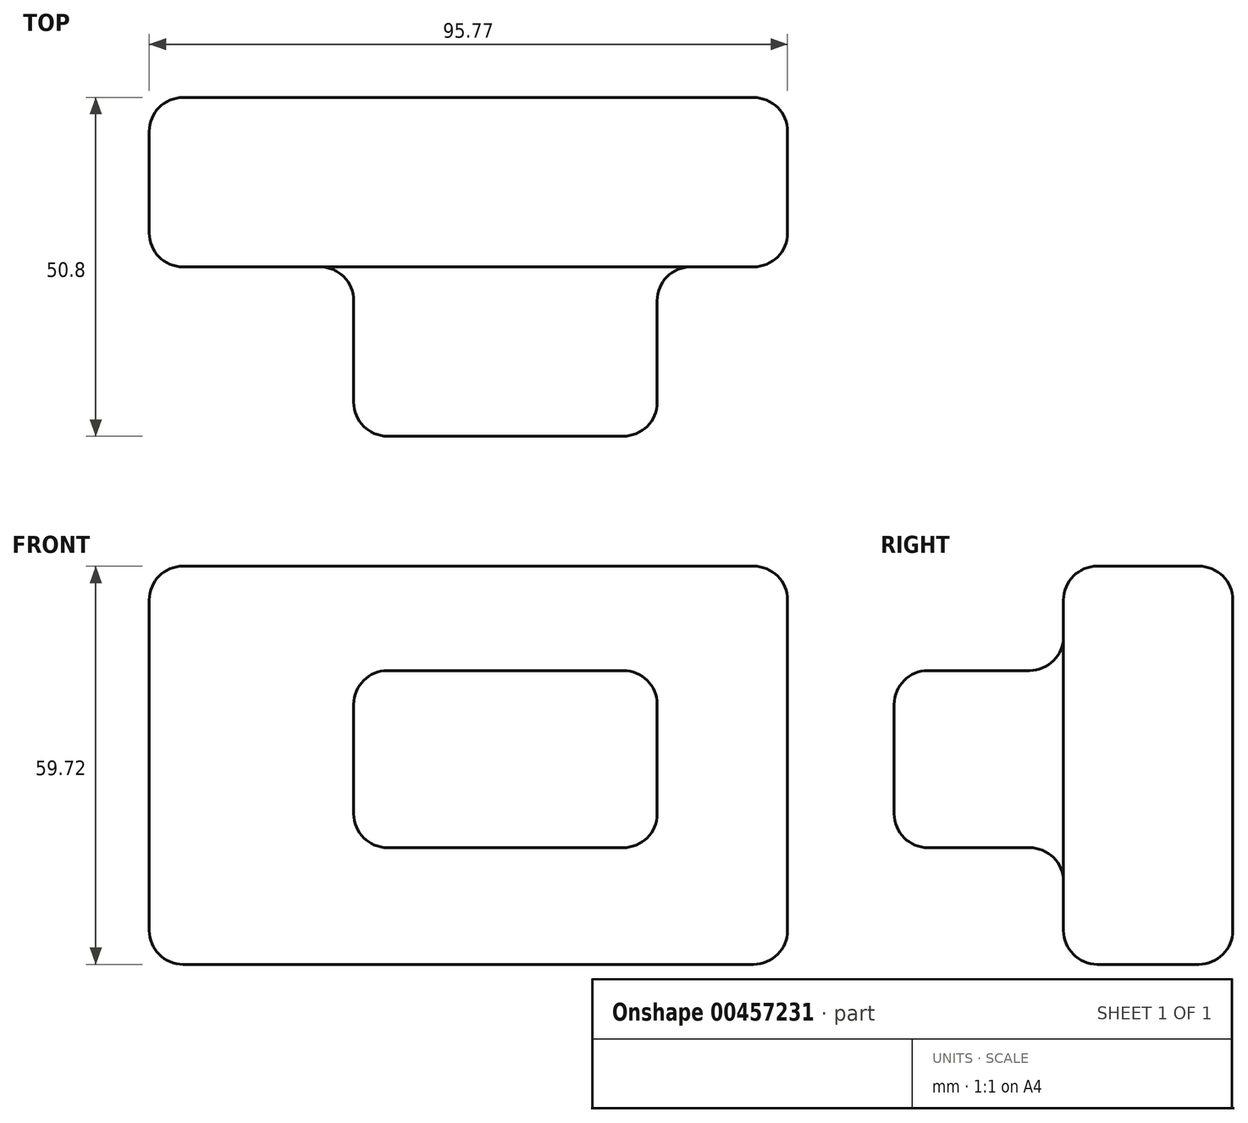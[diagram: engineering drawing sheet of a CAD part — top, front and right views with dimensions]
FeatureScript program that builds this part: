
annotation { "Feature Type Name" : "Feature", "Feature Type Description" : "" }
export const myFeature = defineFeature(function(context is Context, id is Id, definition is map)
    precondition{}
    {
        {
            var Q0;
            Q0=qCreatedBy(makeId("Front.planeOp"),FACE);
            var sketch = newSketch(context, id + "F0", { "sketchPlane" : qUnion([Q0])});
            skLineSegment(sketch, "E0.bottom", {"start": v(-47.04, 25.43) * mm, "end": v(48.73, 25.43) * mm});
            skLineSegment(sketch, "E0.top", {"start": v(-47.04, -34.3) * mm, "end": v(48.73, -34.3) * mm});
            skLineSegment(sketch, "E0.left", {"start": v(-47.04, 25.43) * mm, "end": v(-47.04, -34.3) * mm});
            skLineSegment(sketch, "E0.right", {"start": v(48.73, 25.43) * mm, "end": v(48.73, -34.3) * mm});
            skSolve(sketch);
        }
        {
            var Q0;
            Q0 = qSketchRegion(id + "F0", true);
            extrude(context, id + "F1", {"entities" : qUnion([Q0]), "depth" : 25.4 * mm});
        }
        {
            var Q0;
            Q0=qCreatedBy(makeId("Front.planeOp"),FACE);
            var sketch = newSketch(context, id + "F2", { "sketchPlane" : qUnion([Q0])});
            skLineSegment(sketch, "E1.bottom", {"start": v(-16.35, 9.78) * mm, "end": v(29.16, 9.78) * mm});
            skLineSegment(sketch, "E1.top", {"start": v(-16.35, -16.78) * mm, "end": v(29.16, -16.78) * mm});
            skLineSegment(sketch, "E1.left", {"start": v(-16.35, 9.78) * mm, "end": v(-16.35, -16.78) * mm});
            skLineSegment(sketch, "E1.right", {"start": v(29.16, 9.78) * mm, "end": v(29.16, -16.78) * mm});
            skSolve(sketch);
        }
        {
            var Q0;
            Q0 = qSketchRegion(id + "F2", true);
            extrude(context, id + "F3", {"entities" : qUnion([Q0]), "operationType" : NewBodyOperationType.ADD, "depth" : 50.8 * mm});
        }
        {
            var Q0;
            Q0=makeQuery(id+"F3.opExtrude","SWEPT_EDGE",EDGE,{"disambiguationData":[OSD([sQuery(id+"F2.wireOp",EDGE,"E1.top"),sQuery(id+"F2.wireOp",EDGE,"E1.left")])]});
            var Q1;
            Q1=makeQuery(id+"F3.opExtrude","SWEPT_EDGE",EDGE,{"disambiguationData":[OSD([sQuery(id+"F2.wireOp",EDGE,"E1.top"),sQuery(id+"F2.wireOp",EDGE,"E1.right")])]});
            var Q2;
            Q2=makeQuery(id+"F1.opExtrude","SWEPT_EDGE",EDGE,{"disambiguationData":[OSD([sQuery(id+"F0.wireOp",EDGE,"E0.top"),sQuery(id+"F0.wireOp",EDGE,"E0.right")])]});
            var Q3;
            Q3=makeQuery(id+"F1.opExtrude","SWEPT_EDGE",EDGE,{"disambiguationData":[OSD([sQuery(id+"F0.wireOp",EDGE,"E0.top"),sQuery(id+"F0.wireOp",EDGE,"E0.left")])]});
            var Q4;
            Q4=makeQuery(id+"F1.opExtrude","SWEPT_EDGE",EDGE,{"disambiguationData":[OSD([sQuery(id+"F0.wireOp",EDGE,"E0.bottom"),sQuery(id+"F0.wireOp",EDGE,"E0.right")])]});
            var Q5;
            Q5=makeQuery(id+"F3.opExtrude","SWEPT_EDGE",EDGE,{"disambiguationData":[OSD([sQuery(id+"F2.wireOp",EDGE,"E1.bottom"),sQuery(id+"F2.wireOp",EDGE,"E1.right")])]});
            var Q6;
            Q6=makeQuery(id+"F1.opExtrude","SWEPT_EDGE",EDGE,{"disambiguationData":[OSD([sQuery(id+"F0.wireOp",EDGE,"E0.bottom"),sQuery(id+"F0.wireOp",EDGE,"E0.left")])]});
            var Q7;
            Q7=makeQuery(id+"F3.opExtrude","SWEPT_EDGE",EDGE,{"disambiguationData":[OSD([sQuery(id+"F2.wireOp",EDGE,"E1.bottom"),sQuery(id+"F2.wireOp",EDGE,"E1.left")])]});
            var Q8;
            Q8=makeQuery(id+"F3.opExtrude","CAP_EDGE",EDGE,{"disambiguationData":[OSD([sQuery(id+"F2.wireOp",EDGE,"E1.bottom")])],"isStart":false});
            var Q9;
            Q9=makeQuery(id+"F3.opExtrude","CAP_EDGE",EDGE,{"disambiguationData":[OSD([sQuery(id+"F2.wireOp",EDGE,"E1.top")])],"isStart":false});
            var Q10;
            Q10=makeQuery(id+"F1.opExtrude","CAP_EDGE",EDGE,{"disambiguationData":[OSD([sQuery(id+"F0.wireOp",EDGE,"E0.bottom")])],"isStart":false});
            var Q11;
            Q11=makeQuery(id+"F1.opExtrude","CAP_EDGE",EDGE,{"disambiguationData":[OSD([sQuery(id+"F0.wireOp",EDGE,"E0.left")])],"isStart":false});
            var Q12;
            Q12=makeQuery(id+"F1.opExtrude","CAP_EDGE",EDGE,{"disambiguationData":[OSD([sQuery(id+"F0.wireOp",EDGE,"E0.top")])],"isStart":false});
            var Q13;
            Q13=makeQuery(id+"F1.opExtrude","CAP_EDGE",EDGE,{"disambiguationData":[OSD([sQuery(id+"F0.wireOp",EDGE,"E0.left")])],"isStart":true});
            var Q14;
            Q14=makeQuery(id+"F1.opExtrude","CAP_EDGE",EDGE,{"disambiguationData":[OSD([sQuery(id+"F0.wireOp",EDGE,"E0.right")])],"isStart":true});
            var Q15;
            Q15=makeQuery(id+"F1.opExtrude","CAP_EDGE",EDGE,{"disambiguationData":[OSD([sQuery(id+"F0.wireOp",EDGE,"E0.top")])],"isStart":true});
            var Q16;
            Q16=makeQuery(id+"F1.opExtrude","CAP_EDGE",EDGE,{"disambiguationData":[OSD([sQuery(id+"F0.wireOp",EDGE,"E0.bottom")])],"isStart":true});
            var Q17;
            Q17=makeQuery(id+"F1.opExtrude","CAP_EDGE",EDGE,{"disambiguationData":[OSD([sQuery(id+"F0.wireOp",EDGE,"E0.right")])],"isStart":false});
            var Q18;
            Q18=makeQuery(id+"F3.opExtrude","CAP_EDGE",EDGE,{"disambiguationData":[OSD([sQuery(id+"F2.wireOp",EDGE,"E1.right")])],"isStart":false});
            var Q19;
            Q19=makeQuery(id+"F3.boolean.opBoolean","INTERSECT",EDGE,{"derivedFrom":[makeQuery(id+"F1.opExtrude","CAP_FACE",FACE,{"disambiguationData":[OSD([sQuery(id+"F0.wireOp",EDGE,"E0.bottom"),sQuery(id+"F0.wireOp",EDGE,"E0.top"),sQuery(id+"F0.wireOp",EDGE,"E0.left"),sQuery(id+"F0.wireOp",EDGE,"E0.right")])],"isStart":false}),makeQuery(id+"F3.opExtrude","SWEPT_FACE",FACE,{"disambiguationData":[OSD([sQuery(id+"F2.wireOp",EDGE,"E1.top")])]})]});
            var Q20;
            Q20=makeQuery(id+"F3.boolean.opBoolean","INTERSECT",EDGE,{"derivedFrom":[makeQuery(id+"F1.opExtrude","CAP_FACE",FACE,{"disambiguationData":[OSD([sQuery(id+"F0.wireOp",EDGE,"E0.bottom"),sQuery(id+"F0.wireOp",EDGE,"E0.top"),sQuery(id+"F0.wireOp",EDGE,"E0.left"),sQuery(id+"F0.wireOp",EDGE,"E0.right")])],"isStart":false}),makeQuery(id+"F3.opExtrude","SWEPT_FACE",FACE,{"disambiguationData":[OSD([sQuery(id+"F2.wireOp",EDGE,"E1.right")])]})]});
            var Q21;
            Q21=makeQuery(id+"F3.opExtrude","CAP_EDGE",EDGE,{"disambiguationData":[OSD([sQuery(id+"F2.wireOp",EDGE,"E1.left")])],"isStart":false});
            var Q22;
            Q22=makeQuery(id+"F3.boolean.opBoolean","INTERSECT",EDGE,{"derivedFrom":[makeQuery(id+"F1.opExtrude","CAP_FACE",FACE,{"disambiguationData":[OSD([sQuery(id+"F0.wireOp",EDGE,"E0.bottom"),sQuery(id+"F0.wireOp",EDGE,"E0.top"),sQuery(id+"F0.wireOp",EDGE,"E0.left"),sQuery(id+"F0.wireOp",EDGE,"E0.right")])],"isStart":false}),makeQuery(id+"F3.opExtrude","SWEPT_FACE",FACE,{"disambiguationData":[OSD([sQuery(id+"F2.wireOp",EDGE,"E1.bottom")])]})]});
            var Q23;
            Q23=makeQuery(id+"F3.boolean.opBoolean","INTERSECT",EDGE,{"derivedFrom":[makeQuery(id+"F1.opExtrude","CAP_FACE",FACE,{"disambiguationData":[OSD([sQuery(id+"F0.wireOp",EDGE,"E0.bottom"),sQuery(id+"F0.wireOp",EDGE,"E0.top"),sQuery(id+"F0.wireOp",EDGE,"E0.left"),sQuery(id+"F0.wireOp",EDGE,"E0.right")])],"isStart":false}),makeQuery(id+"F3.opExtrude","SWEPT_FACE",FACE,{"disambiguationData":[OSD([sQuery(id+"F2.wireOp",EDGE,"E1.left")])]})]});
            fillet(context, id + "F4", {"entities" : qUnion([Q0, Q1, Q2, Q3, Q4, Q5, Q6, Q7, Q8, Q9, Q10, Q11, Q12, Q13, Q14, Q15, Q16, Q17, Q18, Q19, Q20, Q21, Q22, Q23]), "radius" : 5.08 * mm, "tangentPropagation" : true, "allowEdgeOverflow" : false});
        }
    });
